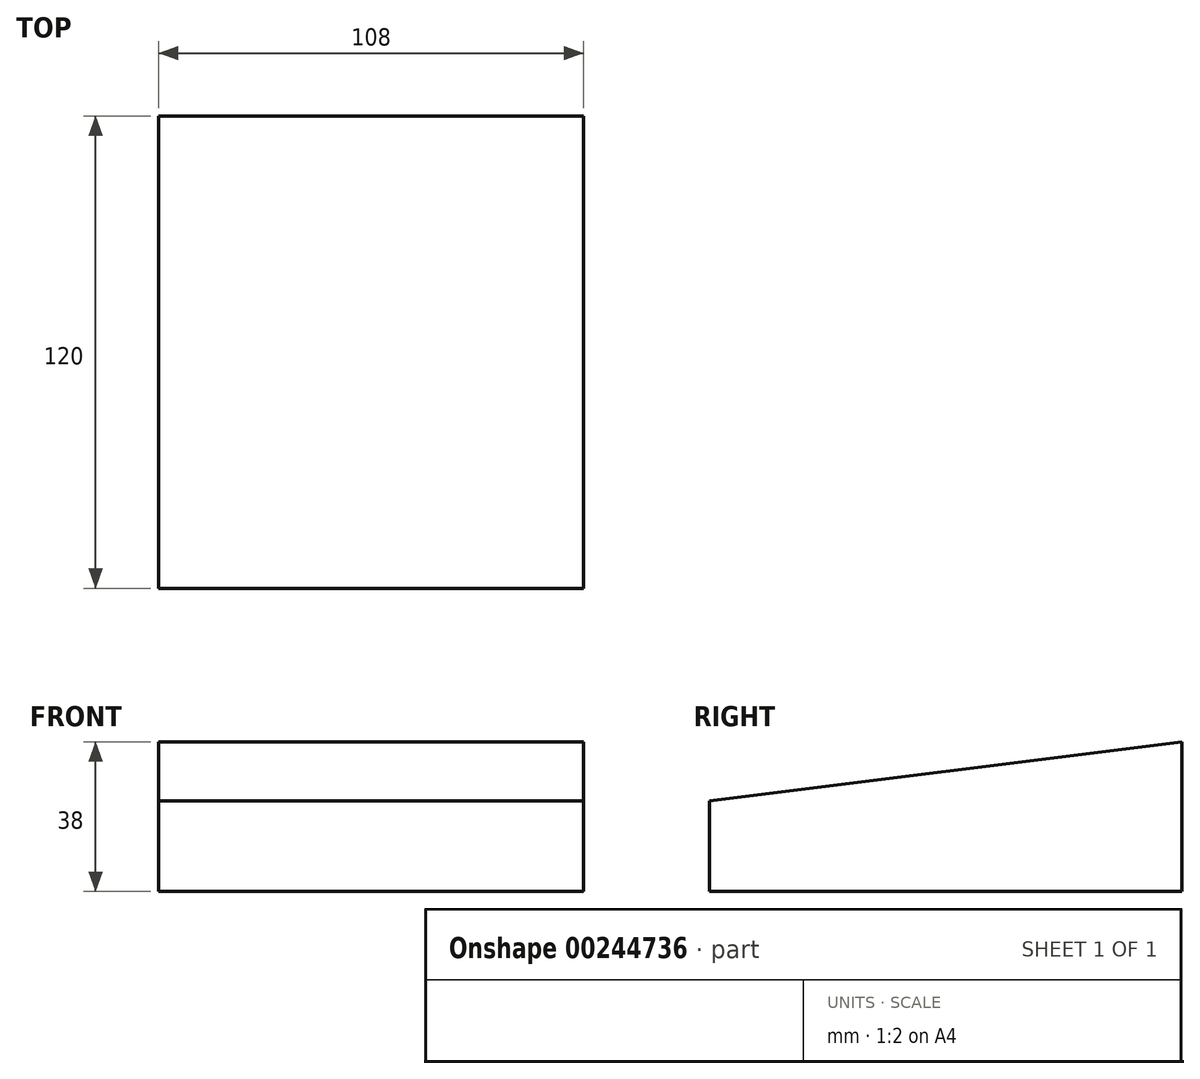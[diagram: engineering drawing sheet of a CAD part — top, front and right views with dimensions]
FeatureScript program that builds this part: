
annotation { "Feature Type Name" : "Feature", "Feature Type Description" : "" }
export const myFeature = defineFeature(function(context is Context, id is Id, definition is map)
    precondition{}
    {
        {
            var Q0;
            Q0=qCreatedBy(makeId("Top.planeOp"),FACE);
            var sketch = newSketch(context, id + "F0", { "sketchPlane" : qUnion([Q0])});
            skLineSegment(sketch, "E0.bottom", {"start": v(-54, 60) * mm, "end": v(54, 60) * mm});
            skLineSegment(sketch, "E0.top", {"start": v(-54, -60) * mm, "end": v(54, -60) * mm});
            skLineSegment(sketch, "E0.left", {"start": v(-54, 60) * mm, "end": v(-54, -60) * mm});
            skLineSegment(sketch, "E0.right", {"start": v(54, 60) * mm, "end": v(54, -60) * mm});
            skPoint(sketch, "E0.middle", {"position": v(0, 0) * mm});
            skLineSegment(sketch, "E1", {"start": v(0, 60) * mm, "end": v(0, -60) * mm});
            skSolve(sketch);
        }
        {
            var Q0;
            {var subQ0=sQuery(id+"F0.wireOp",EDGE,"E0.left");Q0=makeQuery(id+"F0.imprint","IMPRINT",FACE,{"disambiguationData":[TD([[makeQuery(id+"F0.imprint","IMPRINT",EDGE,{"derivedFrom":subQ0}),1.0]])]});}
            var Q1;
            {var subQ0=sQuery(id+"F0.wireOp",EDGE,"E0.right");Q1=makeQuery(id+"F0.imprint","IMPRINT",FACE,{"disambiguationData":[TD([[makeQuery(id+"F0.imprint","IMPRINT",EDGE,{"derivedFrom":subQ0}),-1.0]])]});}
            extrude(context, id + "F1", {"entities" : qUnion([Q0, Q1]), "depth" : 38 * mm});
        }
        {
            var Q0;
            Q0=makeQuery(id+"F1.opExtrude","SWEPT_FACE",FACE,{"disambiguationData":[OSD([sQuery(id+"F0.wireOp",EDGE,"E0.left")])]});
            var sketch = newSketch(context, id + "F2", { "sketchPlane" : qUnion([Q0])});
            skLineSegment(sketch, "E2", {"start": v(60, 0) * mm, "end": v(60, 23) * mm});
            skLineSegment(sketch, "E3", {"start": v(60, 23) * mm, "end": v(-60, 38) * mm});
            skSolve(sketch);
        }
        {
            var Q0;
            {var subQ0=sQuery(id+"F2.wireOp",EDGE,"E3");Q0=makeQuery(id+"F2.imprint","IMPRINT",FACE,{"disambiguationData":[TD([[makeQuery(id+"F2.imprint","IMPRINT",EDGE,{"derivedFrom":subQ0}),-1.0]])]});}
            extrude(context, id + "F3", {"entities" : qUnion([Q0]), "operationType" : NewBodyOperationType.REMOVE, "endBound" : BoundingType.THROUGH_ALL, "oppositeDirection" : true, "depth" : 25 * mm});
        }
    });
